# Revit family: Legrand Transformateur sec HP 100kVA HB4AIAGPA
name_source: partatom
category: Equipement électrique
revit_build: Autodesk Revit 2018 (Build: 20170223_1515(x64)
units: mm (PartAtom-declared; Revit-internal decimal feet)

## family parameters
Basée sur le plan de construction = Non
Cote de connecteur circulaire = Utiliser le diamètre
Couper avec des vides une fois chargée = Non
Numéro OmniClass = 23.80.10.14.11
Partagée = Non
Point de calcul de pièce = Non
Titre OmniClass = Power Transformers
Toujours verticalement = Oui
Type d'élément = Transformateur

## types (1)
- ZUHB4AIAGPA
    Classe d'isolement = 24 kV
    Conditions Générale d'Utilisation = https://export.legrand.com
    Coût = 0 $
    Description = Transformateur sec HP (Haute Performance) ZUHB4AIAGPA
    Enveloppe compatible IP31 = ZUBXS31AM
    Fabricant = Legrand
    Hauteur = 1380mm
    Io = 2%
    Largeur = 1300mm
    Lwa - Puissance acoustique = 51
    Pk at 120°C = 1800 W
    Po = 280 W
    Poids = 950Kg
    Puissance = 100kVA
    R - wheel diameter = 125
    Tension = 20kV/410V
    Tension primaire = 20.00kV
    Tension secondaire = 410V
    URL = www.legrand.fr
    Uk = 6%
    lc - wheel centre line = 520
    profondeur = 600mm
    type = AAoAk
